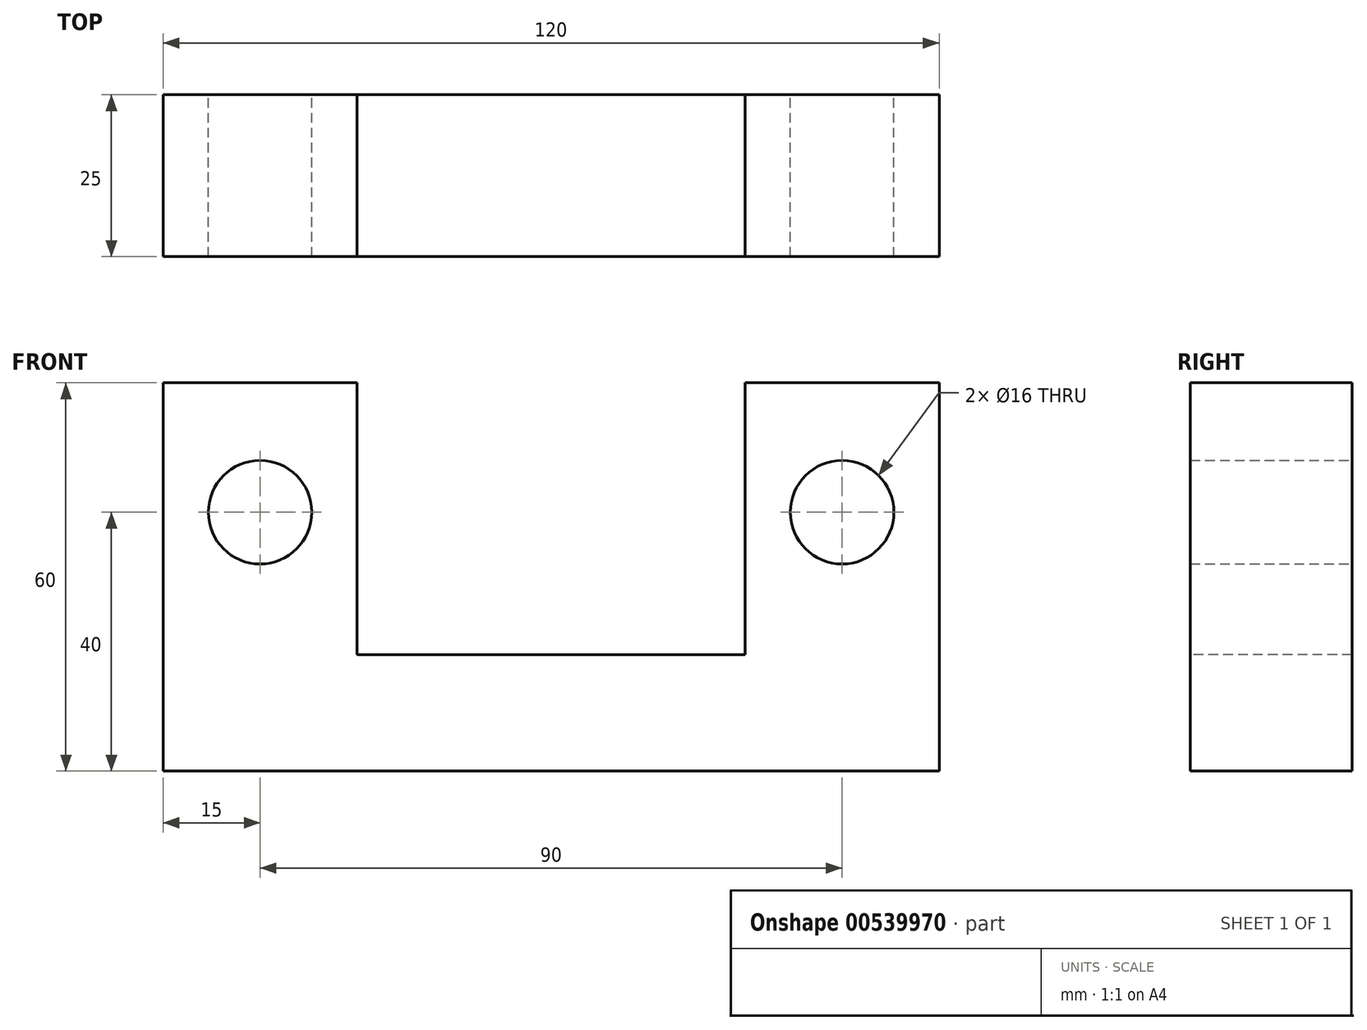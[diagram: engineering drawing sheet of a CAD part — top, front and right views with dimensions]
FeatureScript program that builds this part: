
annotation { "Feature Type Name" : "Feature", "Feature Type Description" : "" }
export const myFeature = defineFeature(function(context is Context, id is Id, definition is map)
    precondition{}
    {
        {
            var Q0;
            Q0=qCreatedBy(makeId("Front.planeOp"),FACE);
            var sketch = newSketch(context, id + "F0", { "sketchPlane" : qUnion([Q0])});
            skLineSegment(sketch, "E0.bottom", {"start": v(0, 0) * mm, "end": v(-60, 0) * mm});
            skLineSegment(sketch, "E0.top", {"start": v(0, 40) * mm, "end": v(-60, 40) * mm});
            skLineSegment(sketch, "E0.left", {"start": v(0, 0) * mm, "end": v(0, 40) * mm});
            skLineSegment(sketch, "E0.right", {"start": v(-60, 0) * mm, "end": v(-60, 40) * mm});
            skLineSegment(sketch, "E1", {"start": v(-60, 20) * mm, "end": v(0, 20) * mm, "construction": true});
            skCircle(sketch, "E2", {"center": v(-45, 20) * mm, "radius": 8 * mm});
            skSolve(sketch);
        }
        {
            var Q0;
            Q0=makeQuery(id+"F0.imprint","IMPRINT",FACE,{"disambiguationData":[TD([[makeQuery(id+"F0.imprint","IMPRINT",EDGE,{"derivedFrom":sQuery(id+"F0.wireOp",EDGE,"E0.bottom")}),-1.0]])]});
            extrude(context, id + "F1", {"entities" : qUnion([Q0]), "depth" : 25 * mm, "offsetDistance" : 25 * mm});
        }
        {
            var Q0;
            Q0=makeQuery(id+"F1.opExtrude","SWEPT_BODY",BODY,{"disambiguationData":[OSD([sQuery(id+"F0.wireOp",EDGE,"E0.bottom"),sQuery(id+"F0.wireOp",EDGE,"E0.top"),sQuery(id+"F0.wireOp",EDGE,"E0.left"),sQuery(id+"F0.wireOp",EDGE,"E0.right"),sQuery(id+"F0.wireOp",EDGE,"E2")])]});
            var Q1;
            Q1=makeQuery(id+"F1.opExtrude","SWEPT_FACE",FACE,{"disambiguationData":[OSD([sQuery(id+"F0.wireOp",EDGE,"E0.left")])]});
            mirror(context, id + "F2", {"operationType" : NewBodyOperationType.ADD, "entities" : qUnion([Q0]), "mirrorPlane" : qUnion([Q1])});
        }
        {
            var Q0;
            {var subQ0=makeQuery(id+"F1.opExtrude","SWEPT_FACE",FACE,{"disambiguationData":[OSD([sQuery(id+"F0.wireOp",EDGE,"E0.bottom")])]});Q0=makeQuery(id+"F2.boolean.opBoolean","MERGE",FACE,{"derivedFrom":[subQ0,makeQuery(id+"F2.opPattern","COPY",FACE,{"derivedFrom":subQ0,"instanceName":"1"})]});}
            extrude(context, id + "F3", {"entities" : qUnion([Q0]), "operationType" : NewBodyOperationType.ADD, "depth" : 20 * mm, "offsetDistance" : 25 * mm});
        }
        {
            var Q0;
            {var subQ0=sQuery(id+"F0.wireOp",EDGE,"E0.bottom");var subQ1=makeQuery(id+"F1.opExtrude","CAP_EDGE",EDGE,{"disambiguationData":[OSD([subQ0])],"isStart":false});var subQ2=makeQuery(id+"F1.opExtrude","CAP_FACE",FACE,{"disambiguationData":[OSD([subQ0,sQuery(id+"F0.wireOp",EDGE,"E0.top"),sQuery(id+"F0.wireOp",EDGE,"E0.left"),sQuery(id+"F0.wireOp",EDGE,"E0.right"),sQuery(id+"F0.wireOp",EDGE,"E2")])],"isStart":false});Q0=makeQuery(id+"F3.boolean.opBoolean","MERGE",FACE,{"derivedFrom":[makeQuery(id+"F2.boolean.opBoolean","MERGE",FACE,{"derivedFrom":[subQ2,makeQuery(id+"F2.opPattern","COPY",FACE,{"derivedFrom":subQ2,"instanceName":"1"})]}),makeQuery(id+"F3.opExtrude","SWEPT_FACE",FACE,{"disambiguationData":[OSD([subQ0]),TDD([makeQuery(id+"F2.boolean.opBoolean","MERGE",EDGE,{"derivedFrom":[subQ1,makeQuery(id+"F2.opPattern","COPY",EDGE,{"derivedFrom":subQ1,"instanceName":"1"})]})])]})]});}
            var sketch = newSketch(context, id + "F4", { "sketchPlane" : qUnion([Q0])});
            skCircle(sketch, "E3", {"center": v(0, 20) * mm, "radius": 5 * mm, "construction": true});
            skLineSegment(sketch, "E4", {"start": v(-45, 20) * mm, "end": v(45, 20) * mm, "construction": true});
            skLineSegment(sketch, "E5", {"start": v(-60, -2) * mm, "end": v(60, -2) * mm, "construction": true});
            skLineSegment(sketch, "E6.bottom", {"start": v(0, -2) * mm, "end": v(30, -2) * mm, "construction": true});
            skLineSegment(sketch, "E6.top", {"start": v(0, 20) * mm, "end": v(30, 20) * mm, "construction": true});
            skLineSegment(sketch, "E6.left", {"start": v(0, -2) * mm, "end": v(0, 20) * mm, "construction": true});
            skLineSegment(sketch, "E6.right", {"start": v(30, -2) * mm, "end": v(30, 20) * mm, "construction": true});
            skLineSegment(sketch, "E7.MirrorCS", {"start": v(-30, -2) * mm, "end": v(-30, 20) * mm, "construction": true});
            skLineSegment(sketch, "E8.bottom", {"start": v(-30, -2) * mm, "end": v(30, -2) * mm});
            skLineSegment(sketch, "E8.top", {"start": v(-30, 40) * mm, "end": v(30, 40) * mm});
            skLineSegment(sketch, "E8.left", {"start": v(-30, -2) * mm, "end": v(-30, 40) * mm});
            skLineSegment(sketch, "E8.right", {"start": v(30, -2) * mm, "end": v(30, 40) * mm});
            skSolve(sketch);
        }
        {
            var Q0;
            Q0=makeQuery(id+"F4.imprint","IMPRINT",FACE,{"disambiguationData":[TD([[makeQuery(id+"F4.imprint","IMPRINT",EDGE,{"derivedFrom":sQuery(id+"F4.wireOp",EDGE,"E8.bottom")}),1.0]])]});
            extrude(context, id + "F5", {"entities" : qUnion([Q0]), "operationType" : NewBodyOperationType.REMOVE, "endBound" : BoundingType.THROUGH_ALL, "oppositeDirection" : true, "depth" : 25 * mm, "offsetDistance" : 25 * mm});
        }
    });
